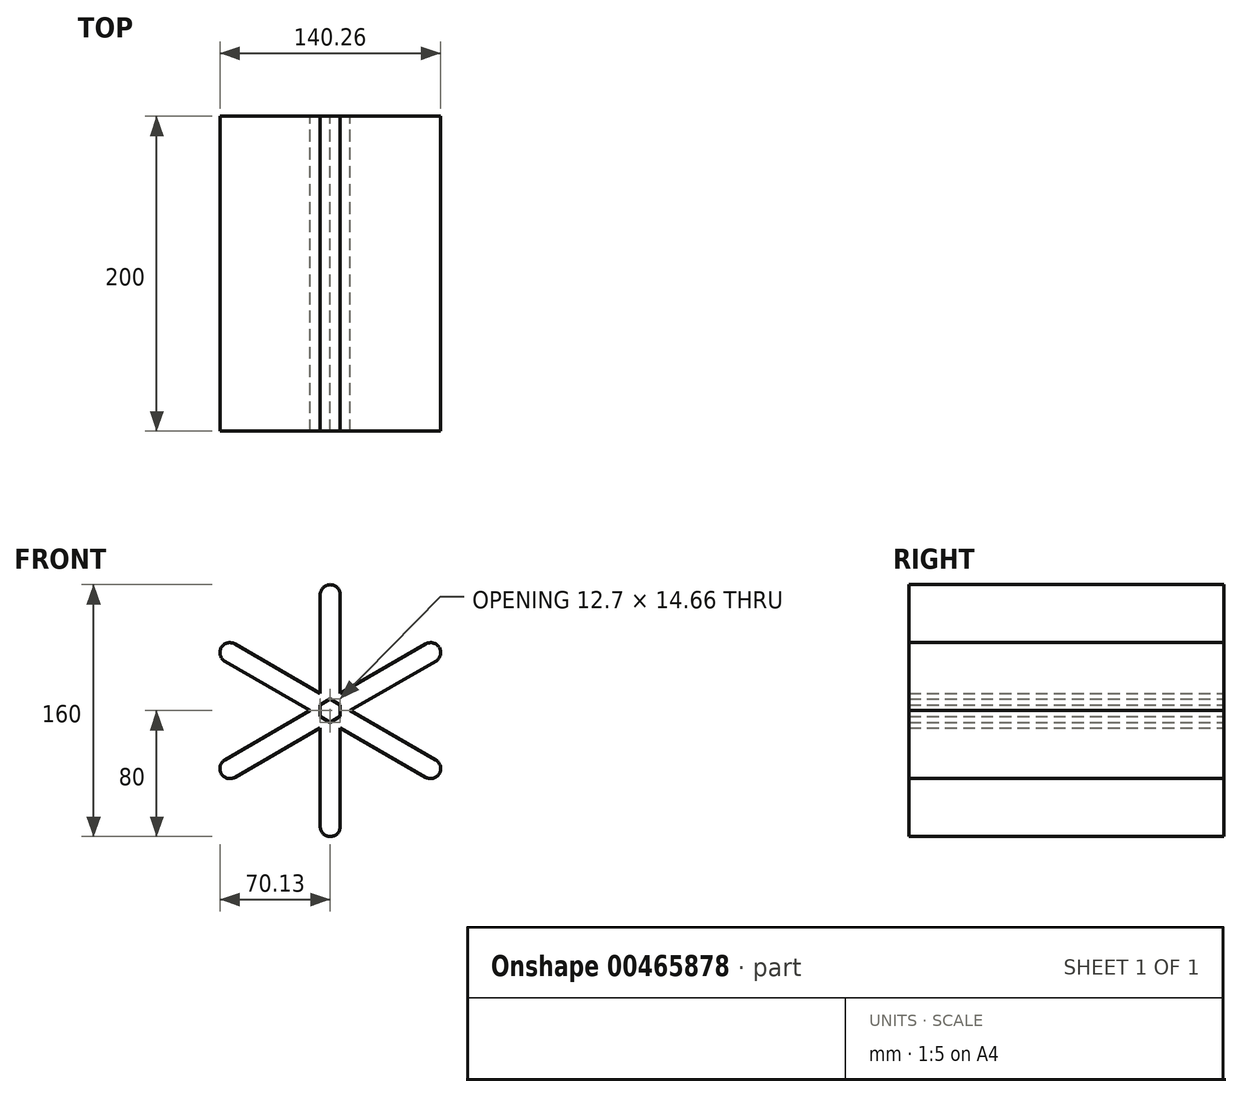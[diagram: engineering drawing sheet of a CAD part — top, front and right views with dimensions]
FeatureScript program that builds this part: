
annotation { "Feature Type Name" : "Feature", "Feature Type Description" : "" }
export const myFeature = defineFeature(function(context is Context, id is Id, definition is map)
    precondition{}
    {
        {
            var Q0;
            Q0=qCreatedBy(makeId("Front.planeOp"),FACE);
            var sketch = newSketch(context, id + "F0", { "sketchPlane" : qUnion([Q0])});
            skLineSegment(sketch, "E0", {"start": v(0, 0) * mm, "end": v(0, -73.65) * mm});
            skLineSegment(sketch, "E1", {"start": v(0, 0) * mm, "end": v(0, 73.65) * mm});
            skLineSegment(sketch, "E2", {"start": v(0, 0) * mm, "end": v(-63.78, -36.82) * mm});
            skLineSegment(sketch, "E3", {"start": v(0, 0) * mm, "end": v(63.78, -36.82) * mm});
            skLineSegment(sketch, "E4", {"start": v(0, 0) * mm, "end": v(-63.78, 36.83) * mm});
            skLineSegment(sketch, "E5", {"start": v(0, 0) * mm, "end": v(63.78, 36.83) * mm});
            skArc(sketch, "E6.0.startCap", {"start": v(3.17, -5.5) * mm, "mid": v(-5.5, -3.18) * mm, "end": v(-3.18, 5.5) * mm});
            skArc(sketch, "E6.0.endCap", {"start": v(60.6, 42.32) * mm, "mid": v(69.28, 40) * mm, "end": v(66.96, 31.33) * mm});
            skLineSegment(sketch, "E6.0.left", {"start": v(-3.18, 5.5) * mm, "end": v(60.6, 42.32) * mm});
            skLineSegment(sketch, "E6.0.right", {"start": v(3.17, -5.5) * mm, "end": v(66.96, 31.33) * mm});
            skArc(sketch, "E7.0.startCap", {"start": v(6.35, 0) * mm, "mid": v(0, -6.35) * mm, "end": v(-6.35, 0) * mm});
            skArc(sketch, "E7.0.endCap", {"start": v(-6.35, 73.65) * mm, "mid": v(0, 80) * mm, "end": v(6.35, 73.65) * mm});
            skLineSegment(sketch, "E7.0.left", {"start": v(-6.35, 0) * mm, "end": v(-6.35, 73.65) * mm});
            skLineSegment(sketch, "E7.0.right", {"start": v(6.35, 0) * mm, "end": v(6.35, 73.65) * mm});
            skArc(sketch, "E7.1.startCap", {"start": v(3.18, 5.5) * mm, "mid": v(5.5, -3.18) * mm, "end": v(-3.17, -5.5) * mm});
            skArc(sketch, "E7.1.endCap", {"start": v(-66.96, 31.33) * mm, "mid": v(-69.28, 40) * mm, "end": v(-60.6, 42.32) * mm});
            skLineSegment(sketch, "E7.1.left", {"start": v(-3.17, -5.5) * mm, "end": v(-66.96, 31.33) * mm});
            skLineSegment(sketch, "E7.1.right", {"start": v(3.18, 5.5) * mm, "end": v(-60.6, 42.32) * mm});
            skArc(sketch, "E7.2.startCap", {"start": v(-3.18, 5.5) * mm, "mid": v(5.5, 3.17) * mm, "end": v(3.17, -5.5) * mm});
            skArc(sketch, "E7.2.endCap", {"start": v(-60.6, -42.32) * mm, "mid": v(-69.28, -40) * mm, "end": v(-66.96, -31.33) * mm});
            skLineSegment(sketch, "E7.2.left", {"start": v(3.17, -5.5) * mm, "end": v(-60.6, -42.32) * mm});
            skLineSegment(sketch, "E7.2.right", {"start": v(-3.18, 5.5) * mm, "end": v(-66.96, -31.33) * mm});
            skArc(sketch, "E7.3.startCap", {"start": v(-6.35, 0) * mm, "mid": v(0, 6.35) * mm, "end": v(6.35, 0) * mm});
            skArc(sketch, "E7.3.endCap", {"start": v(6.35, -73.65) * mm, "mid": v(0, -80) * mm, "end": v(-6.35, -73.65) * mm});
            skLineSegment(sketch, "E7.3.left", {"start": v(6.35, 0) * mm, "end": v(6.35, -73.65) * mm});
            skLineSegment(sketch, "E7.3.right", {"start": v(-6.35, 0) * mm, "end": v(-6.35, -73.65) * mm});
            skArc(sketch, "E8.0.startCap", {"start": v(-3.18, -5.5) * mm, "mid": v(-5.5, 3.18) * mm, "end": v(3.17, 5.5) * mm});
            skArc(sketch, "E8.0.endCap", {"start": v(66.96, -31.33) * mm, "mid": v(69.28, -40) * mm, "end": v(60.6, -42.32) * mm});
            skLineSegment(sketch, "E8.0.left", {"start": v(3.17, 5.5) * mm, "end": v(66.96, -31.33) * mm});
            skLineSegment(sketch, "E8.0.right", {"start": v(-3.18, -5.5) * mm, "end": v(60.6, -42.32) * mm});
            skSolve(sketch);
        }
        {
            var Q0;
            Q0 = qSketchRegion(id + "F0", true);
            extrude(context, id + "F1", {"entities" : qUnion([Q0]), "depth" : 200 * mm});
        }
    });
